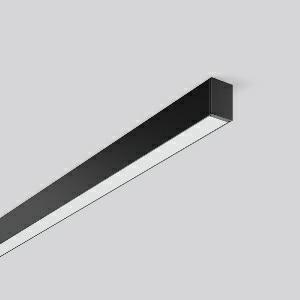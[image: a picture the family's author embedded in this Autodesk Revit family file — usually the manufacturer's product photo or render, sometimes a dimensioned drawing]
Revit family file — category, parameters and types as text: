
# Revit family: less_is_more_27_312196_003_76_11df
name_source: partatom
category: Lighting Fixtures
units: mm (PartAtom-declared; Revit-internal decimal feet)

## family parameters
Cut with Voids When Loaded = No
Host = Face
Light Source = No
Part Type = Normal
Room Calculation Point = No
Round Connector Dimension = Use Diameter
Shared = No

## types (1)
- LESS IS MORE 27 (1 x LED Modul 830, 1600 lm, 3000)
    Apparent Load = 29 VA
    CIE Flux Codes = 48 79 96 100 100
    Color Rendering = 80
    Color Temperature = 3000
    Default Elevation = 1800 mm
    Description = Series: LESS IS MORE 27
Ceiling and wall luminaire with slim design. Housing: extruded aluminium profile, powder-coated. End cap aluminium powder-coated. Diffuser made of non-yellowing plastic (PMMA), opal. Suitable for Ceiling mounting, Wall (surface). External driver with connecting cable. 
Colour: deep black, matt (RAL 9005)
Length: 1012 mm
Width: 28 mm
Height: 38 mm
Lamp: LED
Socket: without socket
Colour temperature: 3000K
Colour rendering index (CRI): 82
System power: 29 W
Rated luminous flux: 1600 lm
Luminous efficiency: 55 lm/W
Control gear: Voltage converter, DALI dim.
Protection class: II
Type of protection: IP 20
    Height = 38 mm
    Lamp = 1 x LED Modul 830
    Lamp Light Flux = 1600 lm
    Lamp count = 1
    Length = 1012 mm
    Lifetime = 50000 h
    Luminous efficacy = 55 lm/W
    Manufacturer = RZB
    ModVariant = No
    Model = 312196.003.76
    Mounting Place = Ceiling, Wall
    Mounting Type = Surface mounted
    Number of Poles = 1
    OnlyDefault = Yes
    Power Factor = 1
    Product Name = LESS IS MORE 27
    Product group = Surface mounted LED linear luminaires
    ProductGroupID = 307
    Protection Class = Protection class II
    Protection Degree = IP 20
    RLX_Detail_Level = 1
    RLX_Emergency_Light_Flux = 0 lm
    RLX_Emergency_Type = 0
    RLX_Emergency_Type_DB = No
    RlxData = <blob elided: 28629 chars, md5=e2b9e9db>
    Socket = socket
    Standby Power = 0 W
    System Light Flux = 1600 lm
    System Power = 29 W
    Type Comments = Product without accessories
    Type Image = 312196.003.jpg
    URL = http://relux.com
    VarID = ---
    Voltage = 230 V
    Voltage Range = 220-240 V
    Weight = 0.00 kg
    Width = 28 mm

## geometry (parser evidence)
native form markers: Blend x4, Sweep x11
no freeform markers — native parametric forms only
